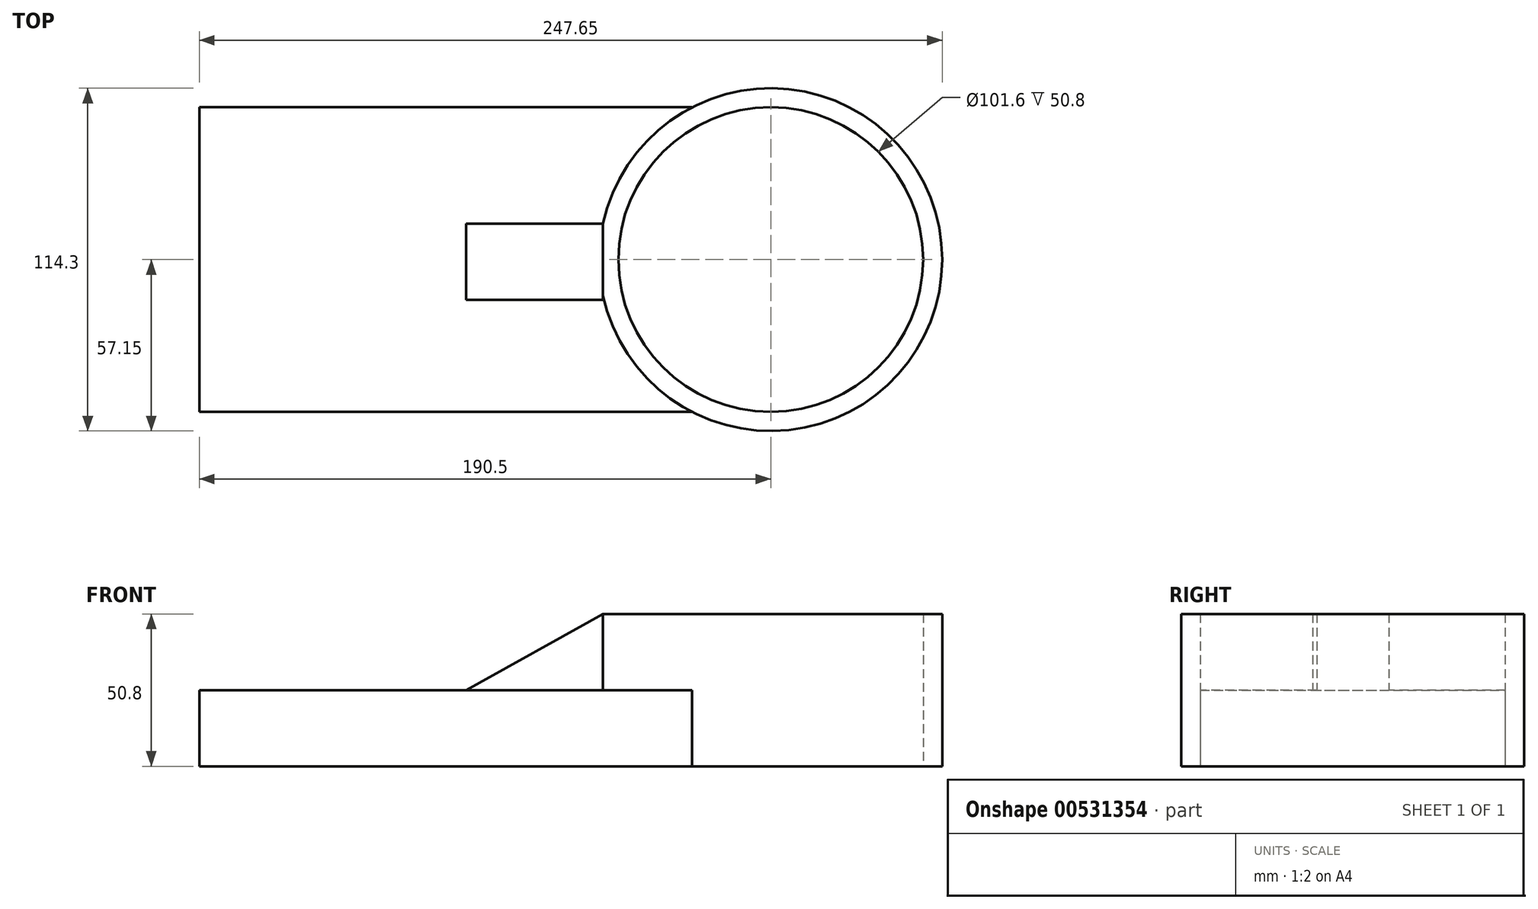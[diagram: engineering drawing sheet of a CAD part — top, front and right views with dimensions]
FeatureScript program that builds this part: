
annotation { "Feature Type Name" : "Feature", "Feature Type Description" : "" }
export const myFeature = defineFeature(function(context is Context, id is Id, definition is map)
    precondition{}
    {
        {
            var Q0;
            Q0=qCreatedBy(makeId("Top.planeOp"),FACE);
            var sketch = newSketch(context, id + "F0", { "sketchPlane" : qUnion([Q0])});
            skLineSegment(sketch, "E0.bottom", {"start": v(88.9, -50.8) * mm, "end": v(-88.9, -50.8) * mm});
            skLineSegment(sketch, "E0.top", {"start": v(88.9, 50.8) * mm, "end": v(-88.9, 50.8) * mm});
            skLineSegment(sketch, "E0.left", {"start": v(88.9, -50.8) * mm, "end": v(88.9, 50.8) * mm});
            skLineSegment(sketch, "E0.right", {"start": v(-88.9, -50.8) * mm, "end": v(-88.9, 50.8) * mm});
            skPoint(sketch, "E0.middle", {"position": v(0, 0) * mm});
            skSolve(sketch);
        }
        {
            var Q0;
            Q0=makeQuery(id+"F0.imprint","IMPRINT",FACE,{"disambiguationData":[TD([[makeQuery(id+"F0.imprint","IMPRINT",EDGE,{"derivedFrom":sQuery(id+"F0.wireOp",EDGE,"E0.bottom")}),-1.0]])]});
            extrude(context, id + "F1", {"entities" : qUnion([Q0]), "depth" : 25.4 * mm, "offsetDistance" : 25.4 * mm});
        }
        {
            var Q0;
            Q0=qCreatedBy(makeId("Top.planeOp"),FACE);
            var sketch = newSketch(context, id + "F2", { "sketchPlane" : qUnion([Q0])});
            skCircle(sketch, "E1", {"center": v(101.6, 0) * mm, "radius": 57.15 * mm});
            skCircle(sketch, "E2", {"center": v(101.6, 0) * mm, "radius": 50.8 * mm});
            skSolve(sketch);
        }
        {
            var Q0;
            Q0=makeQuery(id+"F2.imprint","IMPRINT",FACE,{"disambiguationData":[TD([[makeQuery(id+"F2.imprint","IMPRINT",EDGE,{"derivedFrom":sQuery(id+"F2.wireOp",EDGE,"E1")}),1.0]])]});
            extrude(context, id + "F3", {"entities" : qUnion([Q0]), "operationType" : NewBodyOperationType.ADD, "depth" : 50.8 * mm, "offsetDistance" : 25.4 * mm});
        }
        {
            var Q0;
            Q0 = qSketchRegion(id + "F2", true);
            var Q1;
            {var subQ0=sQuery(id+"F0.wireOp",EDGE,"E0.left");Q1=makeQuery(id+"F3.boolean.opBoolean","SPLIT",FACE,{"disambiguationData":[TD([makeQuery(id+"F1.opExtrude","SWEPT_FACE",FACE,{"disambiguationData":[OSD([subQ0])]})])],"derivedFrom":makeQuery(id+"F1.opExtrude","CAP_FACE",FACE,{"disambiguationData":[OSD([sQuery(id+"F0.wireOp",EDGE,"E0.bottom"),sQuery(id+"F0.wireOp",EDGE,"E0.top"),subQ0,sQuery(id+"F0.wireOp",EDGE,"E0.right")])],"isStart":false})});}
            extrude(context, id + "F4", {"entities" : qUnion([Q0, Q1]), "operationType" : NewBodyOperationType.REMOVE, "oppositeDirection" : true, "depth" : 25.4 * mm, "offsetDistance" : 25.4 * mm});
        }
        {
            var Q0;
            {var subQ0=sQuery(id+"F0.wireOp",EDGE,"E0.bottom");var subQ1=sQuery(id+"F0.wireOp",EDGE,"E0.right");var subQ2=sQuery(id+"F0.wireOp",EDGE,"E0.top");Q0=makeQuery(id+"F3.boolean.opBoolean","SPLIT",FACE,{"disambiguationData":[TD([makeQuery(id+"F1.opExtrude","SWEPT_FACE",FACE,{"disambiguationData":[OSD([subQ0])]})])],"derivedFrom":makeQuery(id+"F1.opExtrude","CAP_FACE",FACE,{"disambiguationData":[OSD([subQ0,subQ2,sQuery(id+"F0.wireOp",EDGE,"E0.left"),subQ1])],"isStart":false})});}
            var sketch = newSketch(context, id + "F5", { "sketchPlane" : qUnion([Q0])});
            skLineSegment(sketch, "E3.bottom", {"start": v(0, -13.42) * mm, "end": v(45.72, -13.42) * mm});
            skLineSegment(sketch, "E3.top", {"start": v(0, 11.98) * mm, "end": v(45.72, 11.98) * mm});
            skLineSegment(sketch, "E3.left", {"start": v(0, -13.42) * mm, "end": v(0, 11.98) * mm});
            skLineSegment(sketch, "E3.right", {"start": v(45.72, -13.42) * mm, "end": v(45.72, 11.98) * mm});
            skSolve(sketch);
        }
        {
            var Q0;
            {var subQ1=sQuery(id+"F5.wireOp",EDGE,"E3.bottom");Q0=makeQuery(id+"F5.imprint","IMPRINT",FACE,{"disambiguationData":[TD([[makeQuery(id+"F5.imprint","IMPRINT",EDGE,{"derivedFrom":subQ1}),1.0]])]});}
            extrude(context, id + "F6", {"entities" : qUnion([Q0]), "operationType" : NewBodyOperationType.ADD, "depth" : 25.4 * mm, "offsetDistance" : 25.4 * mm});
        }
        {
            var Q0;
            Q0=makeQuery(id+"F6.opExtrude","SWEPT_FACE",FACE,{"disambiguationData":[OSD([sQuery(id+"F5.wireOp",EDGE,"E3.bottom")])]});
            var sketch = newSketch(context, id + "F7", { "sketchPlane" : qUnion([Q0])});
            skLineSegment(sketch, "E4", {"start": v(45.72, 50.8) * mm, "end": v(0, 25.4) * mm});
            skSolve(sketch);
        }
        {
            var Q0;
            Q0 = qSketchRegion(id + "F7", true);
            var Q1;
            Q1=makeQuery(id+"F7.imprint","IMPRINT",FACE,{"disambiguationData":[TD([[makeQuery(id+"F7.imprint","IMPRINT",EDGE,{"derivedFrom":sQuery(id+"F7.wireOp",EDGE,"E4")}),-1.0]])]});
            extrude(context, id + "F8", {"entities" : qUnion([Q0, Q1]), "operationType" : NewBodyOperationType.REMOVE, "oppositeDirection" : true, "depth" : 25.4 * mm, "offsetDistance" : 25.4 * mm});
        }
    });
